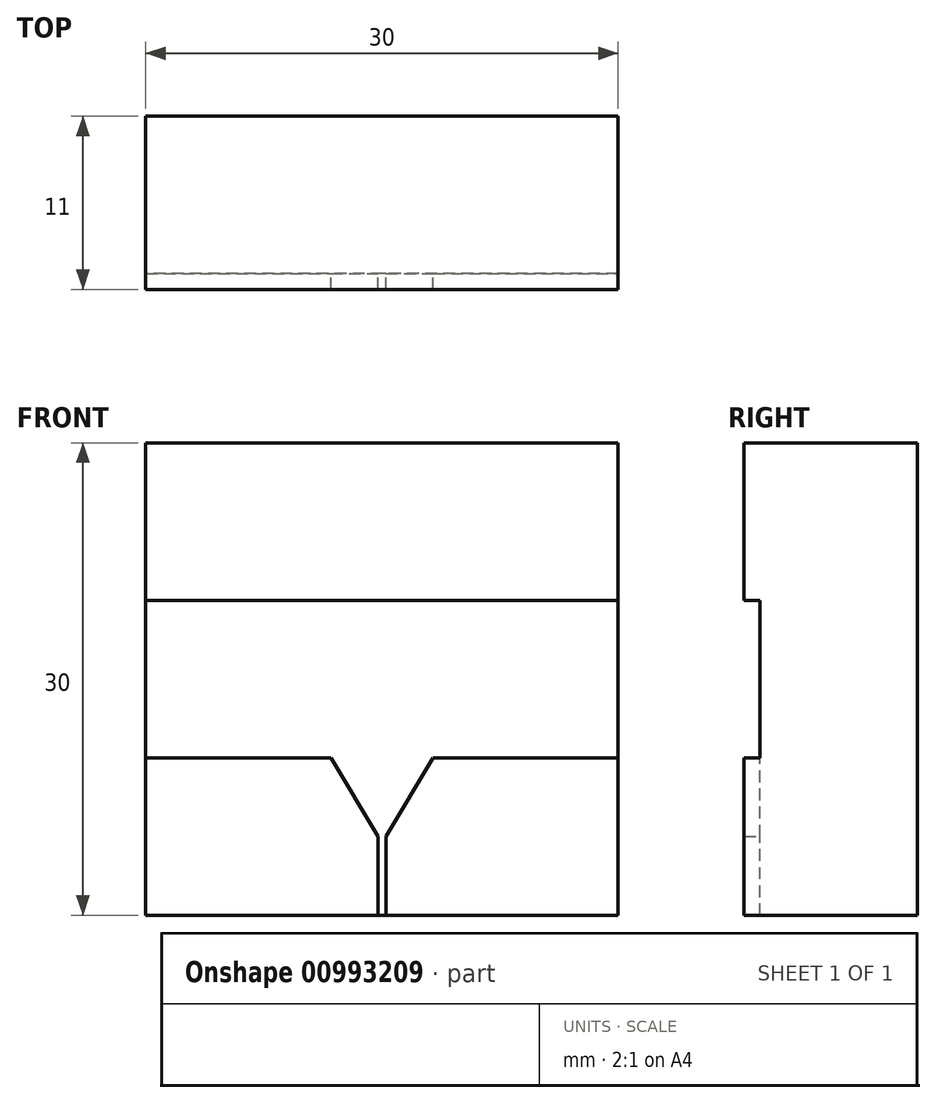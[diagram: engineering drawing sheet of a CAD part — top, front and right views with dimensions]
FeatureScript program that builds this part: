
annotation { "Feature Type Name" : "Feature", "Feature Type Description" : "" }
export const myFeature = defineFeature(function(context is Context, id is Id, definition is map)
    precondition{}
    {
        {
            var Q0;
            Q0=qCreatedBy(makeId("Front.planeOp"),FACE);
            var sketch = newSketch(context, id + "F0", { "sketchPlane" : qUnion([Q0])});
            skLineSegment(sketch, "E0.bottom", {"start": v(15, -15) * mm, "end": v(-15, -15) * mm});
            skLineSegment(sketch, "E0.top", {"start": v(15, 15) * mm, "end": v(-15, 15) * mm});
            skLineSegment(sketch, "E0.left", {"start": v(15, -15) * mm, "end": v(15, 15) * mm});
            skLineSegment(sketch, "E0.right", {"start": v(-15, -15) * mm, "end": v(-15, 15) * mm});
            skPoint(sketch, "E0.middle", {"position": v(0, 0) * mm});
            skSolve(sketch);
        }
        {
            var Q0;
            Q0 = qSketchRegion(id + "F0", true);
            extrude(context, id + "F1", {"entities" : qUnion([Q0]), "depth" : 10 * mm, "offsetDistance" : 25 * mm});
        }
        {
            var Q0;
            Q0=makeQuery(id+"F1.opExtrude","CAP_FACE",FACE,{"disambiguationData":[OSD([sQuery(id+"F0.wireOp",EDGE,"E0.bottom"),sQuery(id+"F0.wireOp",EDGE,"E0.top"),sQuery(id+"F0.wireOp",EDGE,"E0.left"),sQuery(id+"F0.wireOp",EDGE,"E0.right")])],"isStart":false});
            var sketch = newSketch(context, id + "F2", { "sketchPlane" : qUnion([Q0])});
            skLineSegment(sketch, "E1.bottom", {"start": v(15, 15) * mm, "end": v(-15, 15) * mm});
            skLineSegment(sketch, "E1.top", {"start": v(15, 5) * mm, "end": v(-15, 5) * mm});
            skLineSegment(sketch, "E1.left", {"start": v(15, 15) * mm, "end": v(15, 5) * mm});
            skLineSegment(sketch, "E1.right", {"start": v(-15, 15) * mm, "end": v(-15, 5) * mm});
            skPoint(sketch, "E1.middle", {"position": v(0, 10) * mm});
            skLineSegment(sketch, "E2", {"start": v(-15, -5) * mm, "end": v(-3.25, -5) * mm});
            skLineSegment(sketch, "E3", {"start": v(15, -5) * mm, "end": v(15, -15) * mm});
            skLineSegment(sketch, "E4", {"start": v(15, -15) * mm, "end": v(0.25, -15) * mm});
            skLineSegment(sketch, "E5", {"start": v(-15, -15) * mm, "end": v(-15, -5) * mm});
            skLineSegment(sketch, "E6.left", {"start": v(0.25, -15) * mm, "end": v(0.25, -10) * mm});
            skLineSegment(sketch, "E6.right", {"start": v(-0.25, -15) * mm, "end": v(-0.25, -10) * mm});
            skPoint(sketch, "E6.middle", {"position": v(0, -10) * mm});
            skLineSegment(sketch, "E7.trimOffspring", {"start": v(3.25, -5) * mm, "end": v(15, -5) * mm});
            skLineSegment(sketch, "E8.trimOffspring", {"start": v(-0.25, -15) * mm, "end": v(-15, -15) * mm});
            skLineSegment(sketch, "E9", {"start": v(-3.25, -5) * mm, "end": v(-0.25, -10) * mm});
            skLineSegment(sketch, "E10", {"start": v(0.25, -10) * mm, "end": v(3.25, -5) * mm});
            skPoint(sketch, "E11.orphan", {"position": v(-0.25, -5) * mm});
            skPoint(sketch, "E12.orphan", {"position": v(0.25, -5) * mm});
            skSolve(sketch);
        }
        {
            var Q0;
            Q0 = qSketchRegion(id + "F2", true);
            extrude(context, id + "F3", {"entities" : qUnion([Q0]), "operationType" : NewBodyOperationType.ADD, "depth" : 1 * mm, "offsetDistance" : 25 * mm});
        }
    });
